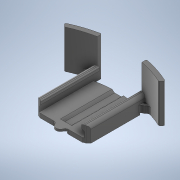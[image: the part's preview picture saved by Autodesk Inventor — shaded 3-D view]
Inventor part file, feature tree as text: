
AUTODESK INVENTOR PART (.ipt)
format: ipt  version: 2020 (Build 240168000, 168)  size: 851,968 bytes
history: native  units: mm
features: projected_geometry x17, other x10, sketch x10, extrude x9, fillet x2, chamfer x1
ambient origin geometry x8: Origin, YZ Plane, XZ Plane, XY Plane, X Axis, Y Axis, Z Axis, Center Point
bodies: Body1 (feature_tree)
feature tree (49):
  other  "Твердое тело1"
  sketch  "Эскиз1"
  other  "РабПлоскость4"
  sketch  "Эскиз2"
  other  "РабПлоскость5"
  sketch  "Эскиз3"
  other  "РабПлоскость6"
  sketch  "Эскиз4"
  other  "РабПлоскость7"
  sketch  "Эскиз5"
  other  "РабПлоскость8"
  sketch  "Эскиз6"
  extrude  "Выдавливание9"  TaperAngle=45.0deg  [1 undecoded]
  extrude  "Выдавливание10"  Depth=7.0mm
  other  "РабПлоскость1"
  extrude  "Выдавливание11"  Depth=20.0mm
  chamfer  "Фаска1"  Distance=7.0mm
  fillet  "Сопряжение1"  Radius=3.2mm
  fillet  "Сопряжение2"  Radius=59.0mm
  other  "РабПлоскость2"
  extrude  "Выдавливание12"  Depth=83.0mm
  other  "РабПлоскость9"
  sketch  "Эскиз9"
  extrude  "Выдавливание13"  Depth=69.0mm
  extrude  "Выдавливание14"  Depth=55.0mm
  other  "РабПлоскость3"
  extrude  "Выдавливание15"  Depth=3.0mm
  extrude  "Выдавливание16"  Depth=8.0mm
  extrude  "Выдавливание17"  Depth=5.0mm
  projected_geometry  "Спроецированная петля1"
  projected_geometry  "Спроецированная петля2"
  projected_geometry  "Спроецированная петля3"
  projected_geometry  "Спроецированная петля4"
  projected_geometry  "Спроецированная петля5"
  sketch  "Эскиз7"
  projected_geometry  "Спроецированная петля6"
  projected_geometry  "Спроецированная петля7"
  projected_geometry  "Спроецированная петля8"
  sketch  "Эскиз8"
  projected_geometry  "Спроецированная петля13"
  projected_geometry  "Спроецированная петля14"
  projected_geometry  "Спроецированная петля15"
  sketch  "Эскиз10"
  projected_geometry  "Спроецированная петля16"
  projected_geometry  "Спроецированная петля18"
  projected_geometry  "Спроецированная петля19"
  projected_geometry  "Спроецированная петля21"
  projected_geometry  "Спроецированная петля24"
  projected_geometry  "Спроецированная петля25"
note: 1 required parameter value undecoded (feature->parameter linkage not recoverable at this tier; creation-order binding heuristic only, values carry confidence <= 0.55)
